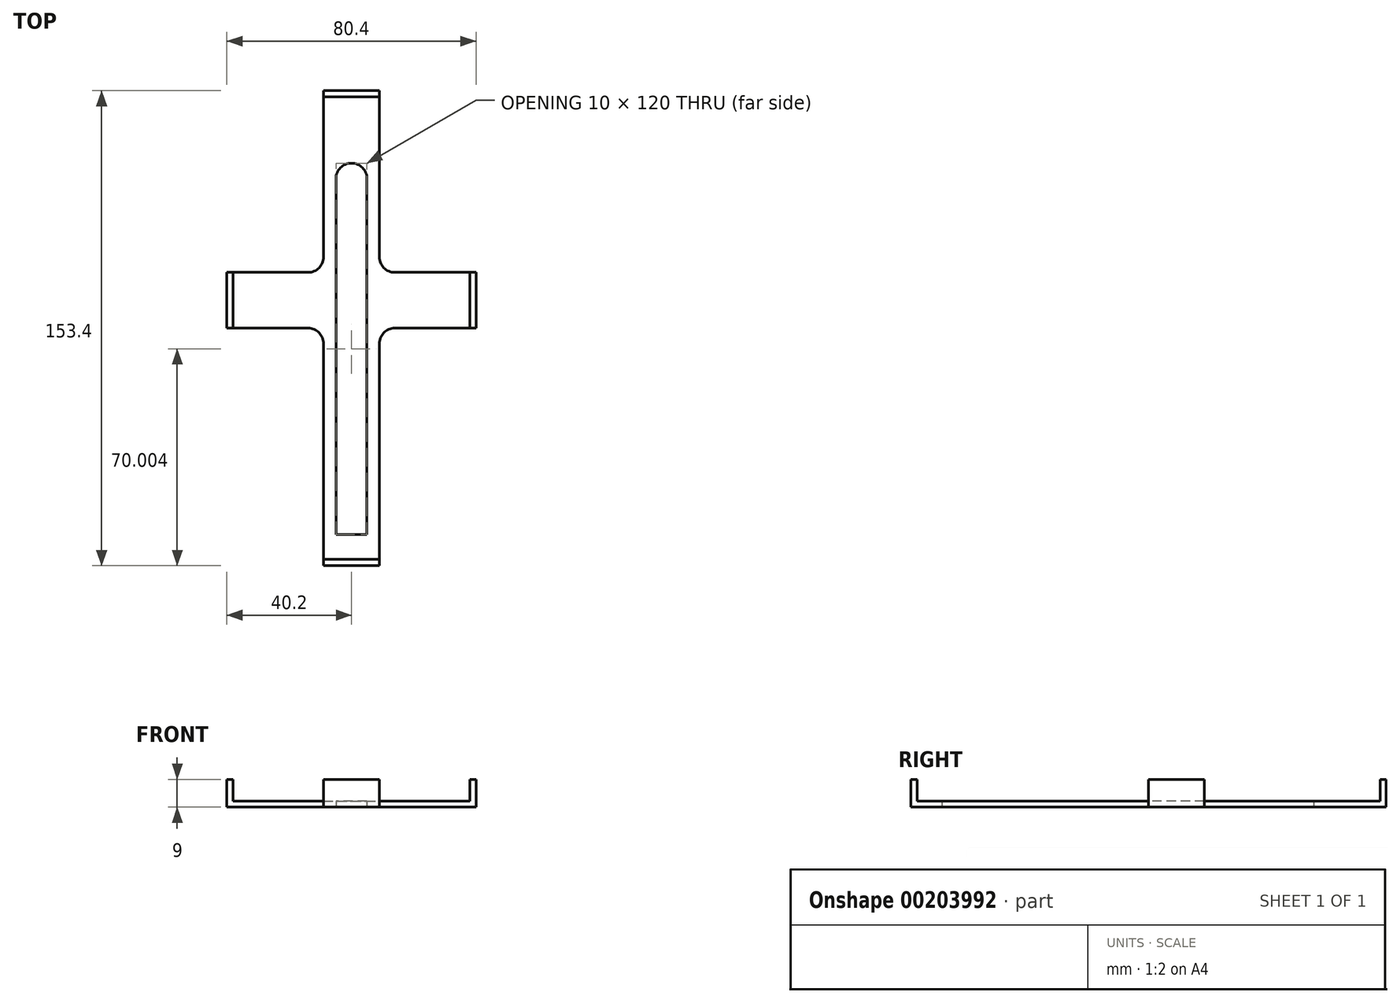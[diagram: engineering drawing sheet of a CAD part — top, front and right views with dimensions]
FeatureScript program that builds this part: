
annotation { "Feature Type Name" : "Feature", "Feature Type Description" : "" }
export const myFeature = defineFeature(function(context is Context, id is Id, definition is map)
    precondition{}
    {
        {
            var Q0;
            Q0=qCreatedBy(makeId("Top.planeOp"),FACE);
            var sketch = newSketch(context, id + "F0", { "sketchPlane" : qUnion([Q0])});
            skLineSegment(sketch, "E0.bottom", {"start": v(-9, 135.37) * mm, "end": v(9, 135.37) * mm});
            skLineSegment(sketch, "E0.top", {"start": v(-9, -18.03) * mm, "end": v(9, -18.03) * mm});
            skLineSegment(sketch, "E0.left", {"start": v(-9, 135.37) * mm, "end": v(-9, -18.03) * mm});
            skLineSegment(sketch, "E0.right", {"start": v(9, 135.37) * mm, "end": v(9, -18.03) * mm});
            skLineSegment(sketch, "E1.bottom", {"start": v(-5, 111.97) * mm, "end": v(5, 111.97) * mm});
            skLineSegment(sketch, "E1.top", {"start": v(-5, -8.03) * mm, "end": v(5, -8.03) * mm});
            skLineSegment(sketch, "E1.left", {"start": v(-5, 111.97) * mm, "end": v(-5, -8.03) * mm});
            skLineSegment(sketch, "E1.right", {"start": v(5, 111.97) * mm, "end": v(5, -8.03) * mm});
            skPoint(sketch, "E2.oppositeSnap0", {"position": v(9, 58.67) * mm});
            skLineSegment(sketch, "E2.bottom", {"start": v(-9, 76.67) * mm, "end": v(-40.2, 76.67) * mm});
            skLineSegment(sketch, "E2.top", {"start": v(-9, 58.67) * mm, "end": v(-40.2, 58.67) * mm});
            skLineSegment(sketch, "E2.left", {"start": v(-9, 76.67) * mm, "end": v(-9, 58.67) * mm});
            skLineSegment(sketch, "E2.right", {"start": v(-40.2, 76.67) * mm, "end": v(-40.2, 58.67) * mm});
            skPoint(sketch, "E3.firstSnap0", {"position": v(-24.6, 76.67) * mm});
            skPoint(sketch, "E3.oppositeSnap0", {"position": v(-24.6, 58.67) * mm});
            skLineSegment(sketch, "E3.bottom", {"start": v(9, 76.67) * mm, "end": v(40.2, 76.67) * mm});
            skLineSegment(sketch, "E3.top", {"start": v(9, 58.67) * mm, "end": v(40.2, 58.67) * mm});
            skLineSegment(sketch, "E3.left", {"start": v(9, 76.67) * mm, "end": v(9, 58.67) * mm});
            skLineSegment(sketch, "E3.right", {"start": v(40.2, 76.67) * mm, "end": v(40.2, 58.67) * mm});
            skSolve(sketch);
        }
        {
            var Q0;
            Q0 = qSketchRegion(id + "F0", true);
            extrude(context, id + "F1", {"entities" : qUnion([Q0]), "depth" : 2 * mm});
        }
        {
            var Q0;
            Q0=makeQuery(id+"F1.opExtrude","CAP_FACE",FACE,{"disambiguationData":[OSD([sQuery(id+"F0.wireOp",EDGE,"E0.bottom"),sQuery(id+"F0.wireOp",EDGE,"E0.top"),sQuery(id+"F0.wireOp",EDGE,"E0.left"),sQuery(id+"F0.wireOp",EDGE,"E0.right"),sQuery(id+"F0.wireOp",EDGE,"E1.bottom"),sQuery(id+"F0.wireOp",EDGE,"E1.top"),sQuery(id+"F0.wireOp",EDGE,"E1.left"),sQuery(id+"F0.wireOp",EDGE,"E1.right"),sQuery(id+"F0.wireOp",EDGE,"E2.bottom"),sQuery(id+"F0.wireOp",EDGE,"E2.top"),sQuery(id+"F0.wireOp",EDGE,"E2.right"),sQuery(id+"F0.wireOp",EDGE,"E3.bottom"),sQuery(id+"F0.wireOp",EDGE,"E3.top"),sQuery(id+"F0.wireOp",EDGE,"E3.right")])],"isStart":false});
            var sketch = newSketch(context, id + "F2", { "sketchPlane" : qUnion([Q0])});
            skSolve(sketch);
        }
        {
            var Q0;
            {var subQ4=sQuery(id+"F0.wireOp",EDGE,"E0.bottom");Q0=makeQuery(id+"F2.imprint","IMPRINT",FACE,{"disambiguationData":[TD([[makeQuery(id+"F2.imprint","IMPRINT",EDGE,{"derivedFrom":makeQuery(id+"F1.opExtrude","CAP_EDGE",EDGE,{"disambiguationData":[OSD([subQ4])],"isStart":false})}),-1.0]])]});}
            var sketch = newSketch(context, id + "F3", { "sketchPlane" : qUnion([Q0])});
            skLineSegment(sketch, "E4.bottom", {"start": v(-40.2, 76.67) * mm, "end": v(-38.2, 76.67) * mm});
            skLineSegment(sketch, "E4.top", {"start": v(-40.2, 58.67) * mm, "end": v(-38.2, 58.67) * mm});
            skLineSegment(sketch, "E4.left", {"start": v(-40.2, 76.67) * mm, "end": v(-40.2, 58.67) * mm});
            skLineSegment(sketch, "E4.right", {"start": v(-38.2, 76.67) * mm, "end": v(-38.2, 58.67) * mm});
            skLineSegment(sketch, "E5.bottom", {"start": v(40.2, 76.67) * mm, "end": v(38.2, 76.67) * mm});
            skLineSegment(sketch, "E5.top", {"start": v(40.2, 58.67) * mm, "end": v(38.2, 58.67) * mm});
            skLineSegment(sketch, "E5.left", {"start": v(40.2, 76.67) * mm, "end": v(40.2, 58.67) * mm});
            skLineSegment(sketch, "E5.right", {"start": v(38.2, 76.67) * mm, "end": v(38.2, 58.67) * mm});
            skLineSegment(sketch, "E6.bottom", {"start": v(-9, 135.37) * mm, "end": v(9, 135.37) * mm});
            skLineSegment(sketch, "E6.top", {"start": v(-9, 133.37) * mm, "end": v(9, 133.37) * mm});
            skLineSegment(sketch, "E6.left", {"start": v(-9, 135.37) * mm, "end": v(-9, 133.37) * mm});
            skLineSegment(sketch, "E6.right", {"start": v(9, 135.37) * mm, "end": v(9, 133.37) * mm});
            skLineSegment(sketch, "E7.bottom", {"start": v(-9, -18.03) * mm, "end": v(9, -18.03) * mm});
            skLineSegment(sketch, "E7.top", {"start": v(-9, -16.03) * mm, "end": v(9, -16.03) * mm});
            skLineSegment(sketch, "E7.left", {"start": v(-9, -18.03) * mm, "end": v(-9, -16.03) * mm});
            skLineSegment(sketch, "E7.right", {"start": v(9, -18.03) * mm, "end": v(9, -16.03) * mm});
            skSolve(sketch);
        }
        {
            var Q0;
            Q0 = qSketchRegion(id + "F3", true);
            extrude(context, id + "F4", {"entities" : qUnion([Q0]), "operationType" : NewBodyOperationType.ADD, "depth" : 7 * mm});
        }
        {
            var Q0;
            Q0=makeQuery(id+"F1.opExtrude","SWEPT_EDGE",EDGE,{"disambiguationData":[OSD([sQuery(id+"F0.wireOp",EDGE,"E0.left"),sQuery(id+"F0.wireOp",EDGE,"E2.top"),sQuery(id+"F0.wireOp",EDGE,"E2.left")])]});
            var Q1;
            Q1=makeQuery(id+"F1.opExtrude","SWEPT_EDGE",EDGE,{"disambiguationData":[OSD([sQuery(id+"F0.wireOp",EDGE,"E0.right"),sQuery(id+"F0.wireOp",EDGE,"E3.top"),sQuery(id+"F0.wireOp",EDGE,"E3.left")])]});
            var Q2;
            Q2=makeQuery(id+"F1.opExtrude","SWEPT_EDGE",EDGE,{"disambiguationData":[OSD([sQuery(id+"F0.wireOp",EDGE,"E0.right"),sQuery(id+"F0.wireOp",EDGE,"E3.bottom"),sQuery(id+"F0.wireOp",EDGE,"E3.left")])]});
            var Q3;
            Q3=makeQuery(id+"F1.opExtrude","SWEPT_EDGE",EDGE,{"disambiguationData":[OSD([sQuery(id+"F0.wireOp",EDGE,"E0.left"),sQuery(id+"F0.wireOp",EDGE,"E2.bottom"),sQuery(id+"F0.wireOp",EDGE,"E2.left")])]});
            var Q4;
            Q4=makeQuery(id+"F1.opExtrude","SWEPT_EDGE",EDGE,{"disambiguationData":[OSD([sQuery(id+"F0.wireOp",EDGE,"E1.bottom"),sQuery(id+"F0.wireOp",EDGE,"E1.left")])]});
            var Q5;
            Q5=makeQuery(id+"F1.opExtrude","SWEPT_EDGE",EDGE,{"disambiguationData":[OSD([sQuery(id+"F0.wireOp",EDGE,"E1.bottom"),sQuery(id+"F0.wireOp",EDGE,"E1.right")])]});
            fillet(context, id + "F5", {"entities" : qUnion([Q0, Q1, Q2, Q3, Q4, Q5]), "radius" : 5 * mm, "tangentPropagation" : true, "allowEdgeOverflow" : false});
        }
    });
